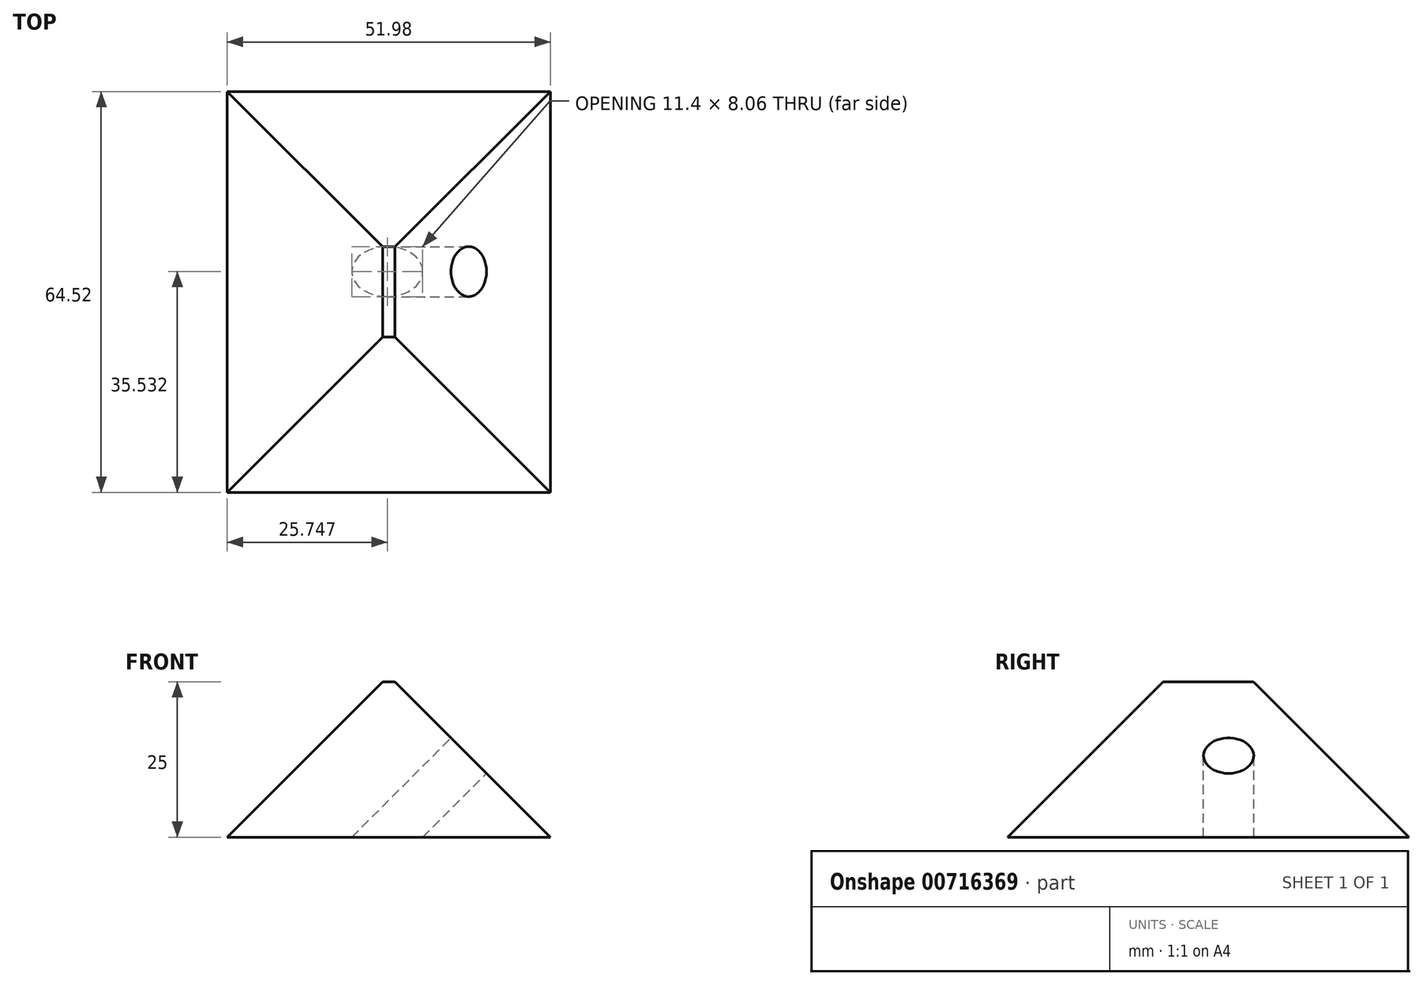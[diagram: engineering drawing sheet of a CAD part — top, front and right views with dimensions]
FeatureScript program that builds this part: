
annotation { "Feature Type Name" : "Feature", "Feature Type Description" : "" }
export const myFeature = defineFeature(function(context is Context, id is Id, definition is map)
    precondition{}
    {
        {
            var Q0;
            Q0=qCreatedBy(makeId("Top.planeOp"),FACE);
            var sketch = newSketch(context, id + "F0", { "sketchPlane" : qUnion([Q0])});
            skLineSegment(sketch, "E0.bottom", {"start": v(0, 0) * mm, "end": v(51.98, 0) * mm});
            skLineSegment(sketch, "E0.top", {"start": v(0, 64.52) * mm, "end": v(51.98, 64.52) * mm});
            skLineSegment(sketch, "E0.left", {"start": v(0, 0) * mm, "end": v(0, 64.52) * mm});
            skLineSegment(sketch, "E0.right", {"start": v(51.98, 0) * mm, "end": v(51.98, 64.52) * mm});
            skSolve(sketch);
        }
        {
            var Q0;
            Q0=makeQuery(id+"F0.imprint","IMPRINT",FACE,{"disambiguationData":[TD([[makeQuery(id+"F0.imprint","IMPRINT",EDGE,{"derivedFrom":sQuery(id+"F0.wireOp",EDGE,"E0.bottom")}),1.0]])]});
            extrude(context, id + "F1", {"entities" : qUnion([Q0]), "depth" : 25 * mm, "offsetDistance" : 25 * mm, "hasDraft" : true, "draftAngle" : 45 * degree, "draftPullDirection" : true});
        }
        {
            var Q0;
            Q0=makeQuery(id+"F1.opExtrude","SWEPT_FACE",FACE,{"disambiguationData":[OSD([sQuery(id+"F0.wireOp",EDGE,"E0.right")])]});
            var sketch = newSketch(context, id + "F2", { "sketchPlane" : qUnion([Q0])});
            skCircle(sketch, "E1", {"center": v(35.53, -18.2) * mm, "radius": 4.03 * mm});
            skSolve(sketch);
        }
        {
            var Q0;
            Q0=makeQuery(id+"F2.imprint","IMPRINT",FACE,{"disambiguationData":[TD([[makeQuery(id+"F2.imprint","IMPRINT",EDGE,{"derivedFrom":sQuery(id+"F2.wireOp",EDGE,"E1")}),1.0]])]});
            extrude(context, id + "F3", {"entities" : qUnion([Q0]), "operationType" : NewBodyOperationType.REMOVE, "oppositeDirection" : true, "depth" : 25 * mm, "offsetDistance" : 25 * mm});
        }
    });
